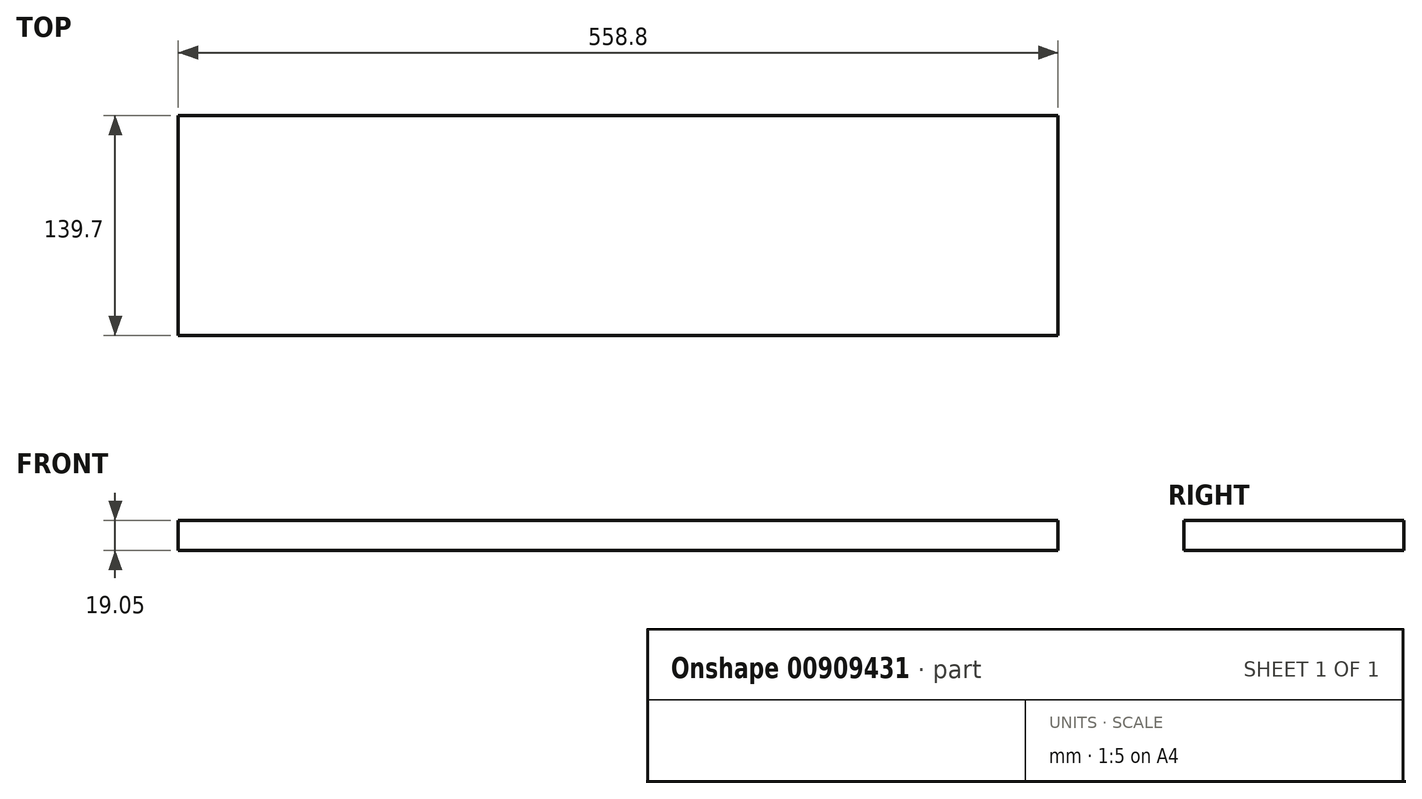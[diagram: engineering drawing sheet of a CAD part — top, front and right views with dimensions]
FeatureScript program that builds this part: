
annotation { "Feature Type Name" : "Feature", "Feature Type Description" : "" }
export const myFeature = defineFeature(function(context is Context, id is Id, definition is map)
    precondition{}
    {
        {
            var Q0;
            Q0=qCreatedBy(makeId("Front.planeOp"),FACE);
            var sketch = newSketch(context, id + "F0", { "sketchPlane" : qUnion([Q0])});
            skLineSegment(sketch, "E0.bottom", {"start": v(0, 19.05) * mm, "end": v(558.8, 19.05) * mm});
            skLineSegment(sketch, "E0.top", {"start": v(0, 0) * mm, "end": v(558.8, 0) * mm});
            skLineSegment(sketch, "E0.left", {"start": v(0, 19.05) * mm, "end": v(0, 0) * mm});
            skLineSegment(sketch, "E0.right", {"start": v(558.8, 19.05) * mm, "end": v(558.8, 0) * mm});
            skSolve(sketch);
        }
        {
            var Q0;
            Q0 = qSketchRegion(id + "F0", true);
            var Q1;
            Q1=makeQuery(id+"F0.imprint","IMPRINT",FACE,{"disambiguationData":[TD([[makeQuery(id+"F0.imprint","IMPRINT",EDGE,{"derivedFrom":sQuery(id+"F0.wireOp",EDGE,"E0.bottom")}),-1.0]])]});
            extrude(context, id + "F1", {"entities" : qUnion([Q0, Q1]), "depth" : 139.7 * mm, "offsetDistance" : 25.4 * mm});
        }
    });
